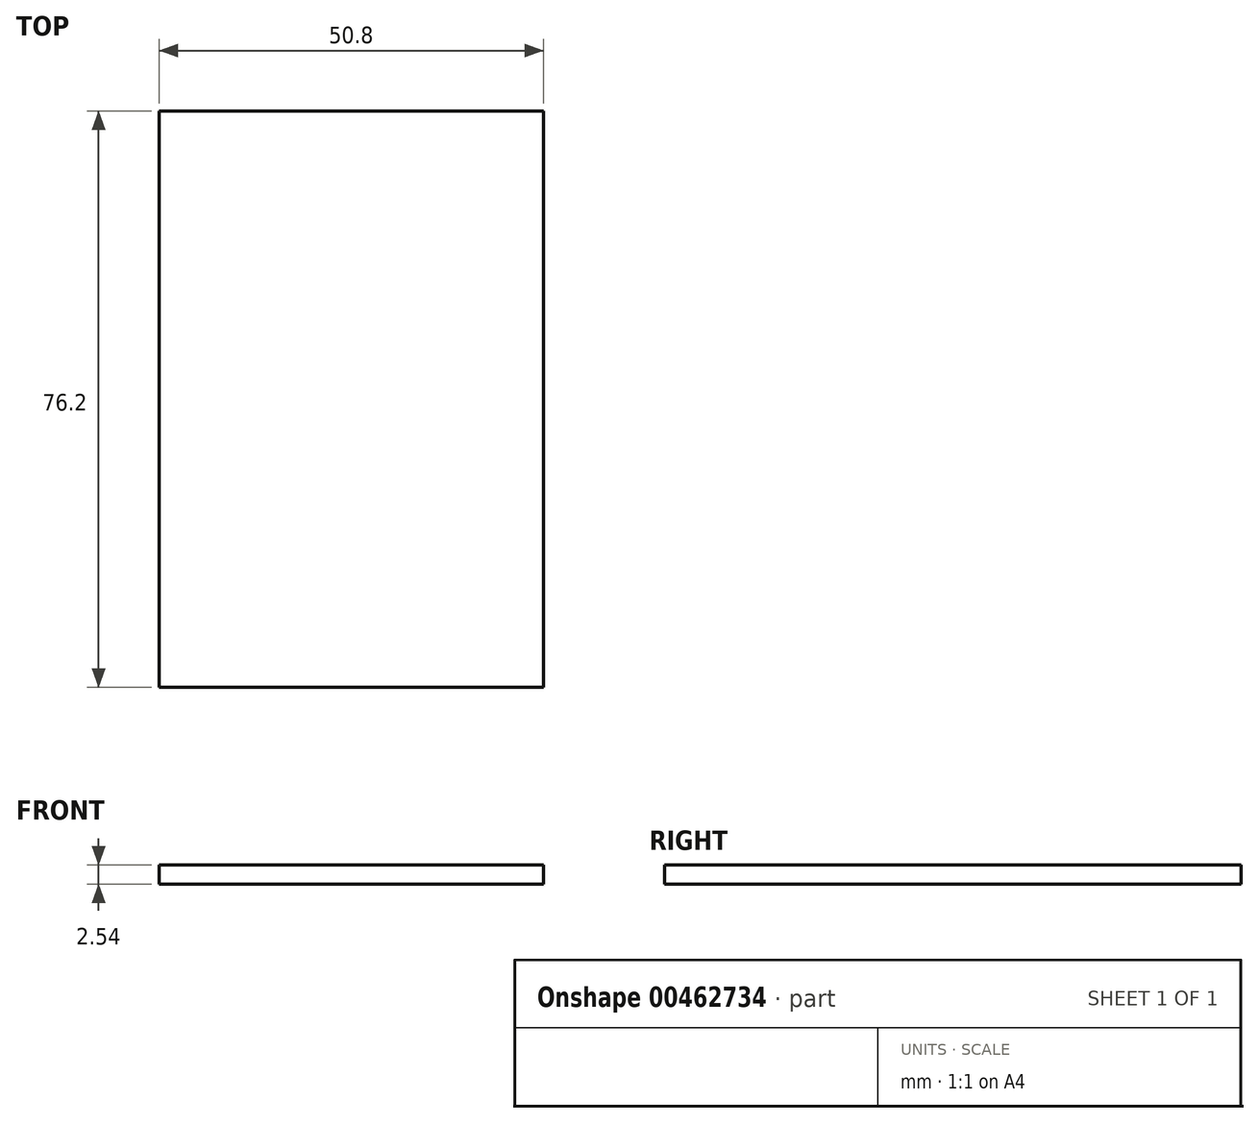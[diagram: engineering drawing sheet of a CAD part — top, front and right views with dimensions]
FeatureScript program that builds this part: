
annotation { "Feature Type Name" : "Feature", "Feature Type Description" : "" }
export const myFeature = defineFeature(function(context is Context, id is Id, definition is map)
    precondition{}
    {
        {
            var Q0;
            Q0=qCreatedBy(makeId("Top.planeOp"),FACE);
            var sketch = newSketch(context, id + "F0", { "sketchPlane" : qUnion([Q0])});
            skLineSegment(sketch, "E0.bottom", {"start": v(-59.64, -49.05) * mm, "end": v(-8.84, -49.05) * mm});
            skLineSegment(sketch, "E0.top", {"start": v(-59.64, 27.15) * mm, "end": v(-8.84, 27.15) * mm});
            skLineSegment(sketch, "E0.left", {"start": v(-59.64, -49.05) * mm, "end": v(-59.64, 27.15) * mm});
            skLineSegment(sketch, "E0.right", {"start": v(-8.84, -49.05) * mm, "end": v(-8.84, 27.15) * mm});
            skSolve(sketch);
        }
        {
            var Q0;
            Q0 = qSketchRegion(id + "F0", true);
            extrude(context, id + "F1", {"entities" : qUnion([Q0]), "depth" : 2.54 * mm});
        }
    });
